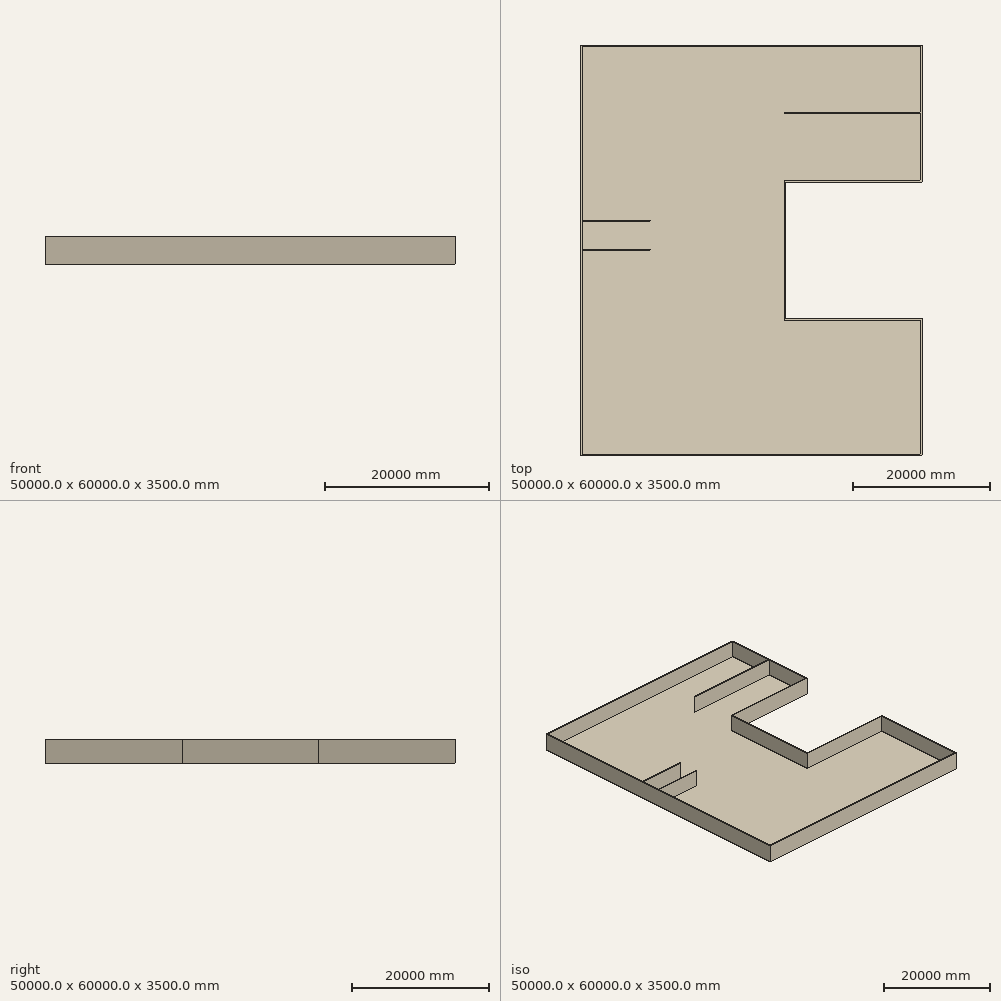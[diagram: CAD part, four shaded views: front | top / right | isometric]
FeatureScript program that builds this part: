
annotation { "Feature Type Name" : "Feature", "Feature Type Description" : "" }
export const myFeature = defineFeature(function(context is Context, id is Id, definition is map)
    precondition{}
    {
        {
            var Q0;
            Q0=qCreatedBy(makeId("Top.planeOp"),FACE);
            var sketch = newSketch(context, id + "F0", { "sketchPlane" : qUnion([Q0])});
            skLineSegment(sketch, "E0.bottom", {"start": v(-50000, 60000) * mm, "end": v(0, 60000) * mm});
            skLineSegment(sketch, "E0.top", {"start": v(-50000, 0) * mm, "end": v(0, 0) * mm});
            skLineSegment(sketch, "E0.left", {"start": v(-50000, 60000) * mm, "end": v(-50000, 0) * mm});
            skLineSegment(sketch, "E0.right", {"start": v(0, 60000) * mm, "end": v(0, 40000) * mm});
            skLineSegment(sketch, "E1", {"start": v(0, 40000) * mm, "end": v(-20000, 40000) * mm});
            skLineSegment(sketch, "E2", {"start": v(-20000, 40000) * mm, "end": v(-20000, 20000) * mm});
            skLineSegment(sketch, "E3", {"start": v(-20000, 20000) * mm, "end": v(0, 20000) * mm});
            skLineSegment(sketch, "E4.trimOffspring", {"start": v(0, 20000) * mm, "end": v(0, 0) * mm});
            skSolve(sketch);
        }
        {
            var Q0;
            Q0 = qSketchRegion(id + "F0", true);
            extrude(context, id + "F1", {"entities" : qUnion([Q0]), "depth" : 3500 * mm, "offsetDistance" : 25.4 * mm});
        }
        {
            var Q0;
            Q0=makeQuery(id+"F1.opExtrude","CAP_FACE",FACE,{"disambiguationData":[OSD([sQuery(id+"F0.wireOp",EDGE,"E0.bottom"),sQuery(id+"F0.wireOp",EDGE,"E0.top"),sQuery(id+"F0.wireOp",EDGE,"E0.left"),sQuery(id+"F0.wireOp",EDGE,"E0.right")])],"isStart":false});
            shell(context, id + "F2", {"entities" : qUnion([Q0]), "thickness" : 200 * mm});
        }
        {
            var Q0;
            Q0=makeQuery(id+"F2.opShell","OFFSET_FACE",FACE,{"disambiguationData":[OSD([sQuery(id+"F0.wireOp",EDGE,"E0.bottom"),sQuery(id+"F0.wireOp",EDGE,"E0.top"),sQuery(id+"F0.wireOp",EDGE,"E0.left"),sQuery(id+"F0.wireOp",EDGE,"E0.right"),sQuery(id+"F0.wireOp",EDGE,"E1"),sQuery(id+"F0.wireOp",EDGE,"E2"),sQuery(id+"F0.wireOp",EDGE,"E3"),sQuery(id+"F0.wireOp",EDGE,"E4.trimOffspring")])]});
            var sketch = newSketch(context, id + "F3", { "sketchPlane" : qUnion([Q0])});
            skLineSegment(sketch, "E5", {"start": v(-200, 50000) * mm, "end": v(-20200, 50000) * mm});
            skLineSegment(sketch, "E6", {"start": v(-20200, 50000) * mm, "end": v(-20200, 50200) * mm});
            skLineSegment(sketch, "E7", {"start": v(-20200, 50200) * mm, "end": v(0, 50200) * mm});
            skLineSegment(sketch, "E8", {"start": v(0, 50200) * mm, "end": v(-200, 50000) * mm});
            skLineSegment(sketch, "E9", {"start": v(-49800, 34200) * mm, "end": v(-39800, 34200) * mm});
            skLineSegment(sketch, "E10", {"start": v(-39800, 30200) * mm, "end": v(-49800, 30200) * mm});
            skLineSegment(sketch, "E11", {"start": v(-49800, 30200) * mm, "end": v(-49800, 34200) * mm});
            skLineSegment(sketch, "E12", {"start": v(-49800, 30200) * mm, "end": v(-49800, 30000) * mm});
            skLineSegment(sketch, "E13", {"start": v(-49800, 30000) * mm, "end": v(-39800, 30000) * mm});
            skLineSegment(sketch, "E14", {"start": v(-39800, 30000) * mm, "end": v(-39800, 30200) * mm});
            skLineSegment(sketch, "E15", {"start": v(-39800, 34400) * mm, "end": v(-49800, 34400) * mm});
            skLineSegment(sketch, "E16", {"start": v(-49800, 34400) * mm, "end": v(-49800, 34200) * mm});
            skLineSegment(sketch, "E17", {"start": v(-39800, 34200) * mm, "end": v(-39800, 34400) * mm});
            skSolve(sketch);
        }
        {
            var Q0;
            Q0 = qSketchRegion(id + "F3", true);
            var Q1;
            Q1=makeQuery(id+"F1.opExtrude","CAP_FACE",FACE,{"disambiguationData":[OSD([sQuery(id+"F0.wireOp",EDGE,"E0.bottom"),sQuery(id+"F0.wireOp",EDGE,"E0.top"),sQuery(id+"F0.wireOp",EDGE,"E0.left"),sQuery(id+"F0.wireOp",EDGE,"E0.right"),sQuery(id+"F0.wireOp",EDGE,"E1"),sQuery(id+"F0.wireOp",EDGE,"E2"),sQuery(id+"F0.wireOp",EDGE,"E3"),sQuery(id+"F0.wireOp",EDGE,"E4.trimOffspring")])],"isStart":false});
            extrude(context, id + "F4", {"entities" : qUnion([Q0]), "operationType" : NewBodyOperationType.ADD, "endBound" : BoundingType.UP_TO_SURFACE, "depth" : 25 * mm, "endBoundEntityFace" : qUnion([Q1]), "offsetDistance" : 25 * mm});
        }
        {
            var Q0;
            Q0=makeQuery(id+"F1.opExtrude","SWEPT_FACE",FACE,{"disambiguationData":[OSD([sQuery(id+"F0.wireOp",EDGE,"E2")])]});
            extrude(context, id + "F5", {"entities" : qUnion([Q0]), "operationType" : NewBodyOperationType.REMOVE, "oppositeDirection" : true, "depth" : 25 * mm, "offsetDistance" : 25 * mm});
        }
    });
